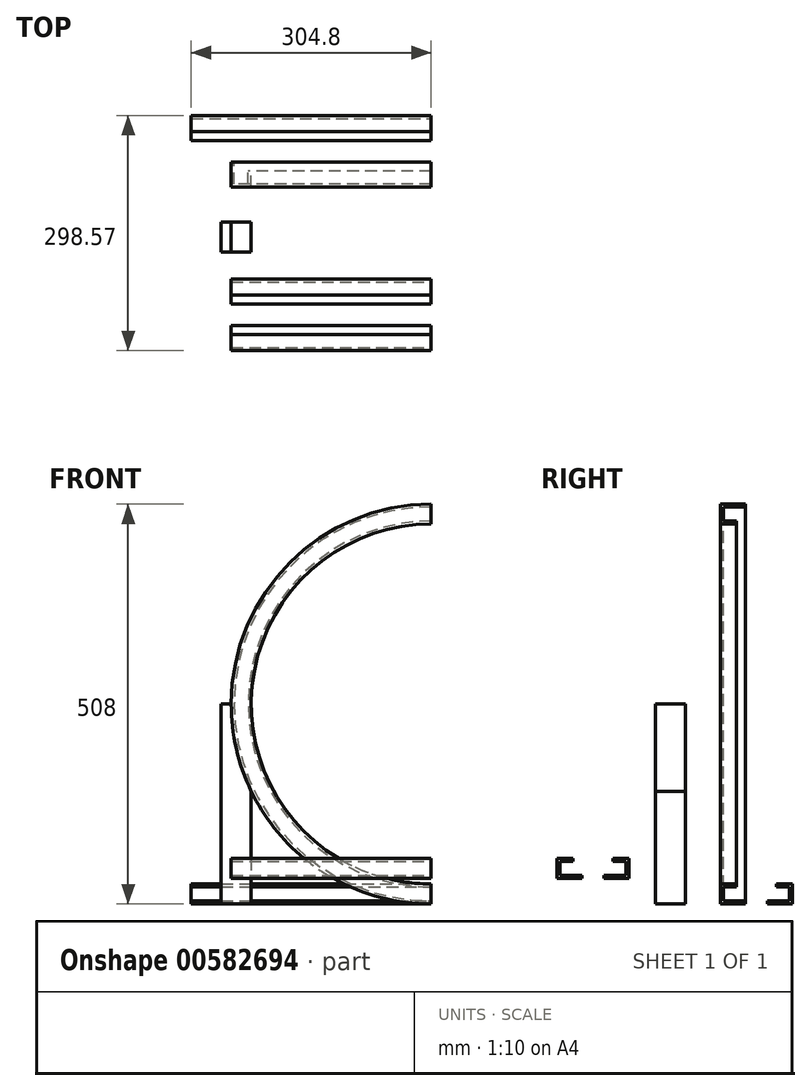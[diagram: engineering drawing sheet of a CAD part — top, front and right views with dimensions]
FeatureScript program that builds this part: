
annotation { "Feature Type Name" : "Feature", "Feature Type Description" : "" }
export const myFeature = defineFeature(function(context is Context, id is Id, definition is map)
    precondition{}
    {
        {
            var Q0;
            Q0=qCreatedBy(makeId("Right.planeOp"),FACE);
            var sketch = newSketch(context, id + "F0", { "sketchPlane" : qUnion([Q0])});
            skLineSegment(sketch, "E0.bottom", {"start": v(-27.94, 21.6) * mm, "end": v(-11.43, 21.6) * mm});
            skLineSegment(sketch, "E0.left", {"start": v(-27.94, 21.6) * mm, "end": v(-27.94, 3.81) * mm});
            skLineSegment(sketch, "E0.right", {"start": v(55.44, 21.6) * mm, "end": v(55.44, 3.81) * mm});
            skLineSegment(sketch, "E1.left", {"start": v(-11.43, 21.6) * mm, "end": v(-11.43, 25.4) * mm});
            skLineSegment(sketch, "E2.bottom", {"start": v(38.93, 25.4) * mm, "end": v(55.44, 25.4) * mm});
            skLineSegment(sketch, "E2.top", {"start": v(38.93, 21.6) * mm, "end": v(55.44, 21.6) * mm});
            skLineSegment(sketch, "E2.left", {"start": v(38.93, 25.4) * mm, "end": v(38.93, 21.6) * mm});
            skLineSegment(sketch, "E3", {"start": v(-11.43, 25.4) * mm, "end": v(-31.75, 25.4) * mm});
            skLineSegment(sketch, "E4", {"start": v(-31.75, 25.4) * mm, "end": v(-31.75, 0) * mm});
            skLineSegment(sketch, "E5", {"start": v(59.25, 0) * mm, "end": v(59.25, 25.4) * mm});
            skLineSegment(sketch, "E6", {"start": v(59.25, 25.4) * mm, "end": v(38.93, 25.4) * mm});
            skLineSegment(sketch, "E7", {"start": v(0, 0) * mm, "end": v(0, 3.81) * mm});
            skLineSegment(sketch, "E8", {"start": v(0, 3.81) * mm, "end": v(-27.94, 3.81) * mm});
            skLineSegment(sketch, "E9", {"start": v(-31.75, 0) * mm, "end": v(0, 0) * mm});
            skLineSegment(sketch, "E10", {"start": v(55.44, 3.81) * mm, "end": v(27.5, 3.81) * mm});
            skLineSegment(sketch, "E11", {"start": v(27.5, 3.81) * mm, "end": v(27.5, 0) * mm});
            skLineSegment(sketch, "E12", {"start": v(27.5, 0) * mm, "end": v(59.25, 0) * mm});
            skSolve(sketch);
        }
        {
            var Q0;
            Q0=qCreatedBy(makeId("Front.planeOp"),FACE);
            var sketch = newSketch(context, id + "F1", { "sketchPlane" : qUnion([Q0])});
            skArc(sketch, "E13", {"start": v(0, 508) * mm, "mid": v(-254, 254) * mm, "end": v(0, 0) * mm});
            skLineSegment(sketch, "E14", {"start": v(0, 254) * mm, "end": v(0, 508) * mm});
            skLineSegment(sketch, "E15", {"start": v(0, 254) * mm, "end": v(-254, 254) * mm});
            skLineSegment(sketch, "E16", {"start": v(0, 254) * mm, "end": v(0, 0) * mm});
            skSolve(sketch);
        }
        {
            var Q0;
            Q0=makeQuery(id+"F0.imprint","IMPRINT",FACE,{"disambiguationData":[TD([[makeQuery(id+"F0.imprint","IMPRINT",EDGE,{"derivedFrom":sQuery(id+"F0.wireOp",EDGE,"E0.bottom")}),1.0]])]});
            var Q1;
            Q1=sQuery(id+"F1.wireOp",EDGE,"E13");
            sweep(context, id + "F2", {"profiles" : qUnion([Q0]), "path" : qUnion([Q1])});
        }
        {
            var Q0;
            Q0=qCreatedBy(makeId("Right.planeOp"),FACE);
            var sketch = newSketch(context, id + "F3", { "sketchPlane" : qUnion([Q0])});
            skLineSegment(sketch, "E17.bottom", {"start": v(-235.5, 53.98) * mm, "end": v(-219, 53.98) * mm});
            skLineSegment(sketch, "E17.left", {"start": v(-235.5, 53.98) * mm, "end": v(-235.5, 36.2) * mm});
            skLineSegment(sketch, "E17.right", {"start": v(-152.13, 53.98) * mm, "end": v(-152.13, 36.2) * mm});
            skLineSegment(sketch, "E18.left", {"start": v(-219, 53.98) * mm, "end": v(-219, 57.8) * mm});
            skLineSegment(sketch, "E19.bottom", {"start": v(-168.64, 57.8) * mm, "end": v(-152.13, 57.8) * mm});
            skLineSegment(sketch, "E19.top", {"start": v(-168.64, 53.98) * mm, "end": v(-152.13, 53.98) * mm});
            skLineSegment(sketch, "E19.left", {"start": v(-168.64, 57.8) * mm, "end": v(-168.64, 53.98) * mm});
            skLineSegment(sketch, "E20", {"start": v(-219, 57.8) * mm, "end": v(-239.32, 57.8) * mm});
            skLineSegment(sketch, "E21", {"start": v(-239.32, 57.8) * mm, "end": v(-239.32, 32.4) * mm});
            skLineSegment(sketch, "E22", {"start": v(-148.32, 32.4) * mm, "end": v(-148.32, 57.8) * mm});
            skLineSegment(sketch, "E23", {"start": v(-148.32, 57.8) * mm, "end": v(-168.64, 57.8) * mm});
            skLineSegment(sketch, "E24", {"start": v(-207.57, 32.4) * mm, "end": v(-207.57, 36.2) * mm});
            skLineSegment(sketch, "E25", {"start": v(-207.57, 36.2) * mm, "end": v(-235.5, 36.2) * mm});
            skLineSegment(sketch, "E26", {"start": v(-239.32, 32.4) * mm, "end": v(-207.57, 32.4) * mm});
            skLineSegment(sketch, "E27", {"start": v(-152.13, 36.2) * mm, "end": v(-180.07, 36.2) * mm});
            skLineSegment(sketch, "E28", {"start": v(-180.07, 36.2) * mm, "end": v(-180.07, 32.4) * mm});
            skLineSegment(sketch, "E29", {"start": v(-180.07, 32.4) * mm, "end": v(-148.32, 32.4) * mm});
            skSolve(sketch);
        }
        {
            var Q0;
            Q0 = qSketchRegion(id + "F3", true);
            extrude(context, id + "F4", {"entities" : qUnion([Q0]), "oppositeDirection" : true, "depth" : 254 * mm, "offsetDistance" : 25.4 * mm});
        }
        {
            var Q0;
            Q0=qCreatedBy(makeId("Front.planeOp"),FACE);
            cPlane(context, id + "F5", {"entities" : qUnion([Q0]), "cplaneType" : CPlaneType.OFFSET, "offset" : 76.2 * mm, "width" : 152.4 * mm, "height" : 152.4 * mm});
        }
        {
            var Q0;
            Q0=qCreatedBy(id+"F5.planeOp",FACE);
            var sketch = newSketch(context, id + "F6", { "sketchPlane" : qUnion([Q0])});
            skLineSegment(sketch, "E30.top", {"start": v(-266.7, 0) * mm, "end": v(-228.6, 0) * mm});
            skLineSegment(sketch, "E30.left", {"start": v(-266.7, 254) * mm, "end": v(-266.7, 0) * mm});
            skLineSegment(sketch, "E30.right", {"start": v(-228.6, 143.28) * mm, "end": v(-228.6, 0) * mm});
            skArc(sketch, "E31", {"start": v(-254, 254) * mm, "mid": v(-247.57, 197.2) * mm, "end": v(-228.6, 143.28) * mm});
            skLineSegment(sketch, "E32", {"start": v(-254, 254) * mm, "end": v(-266.7, 254) * mm});
            skSolve(sketch);
        }
        {
            var Q0;
            Q0=makeQuery(id+"F6.imprint","IMPRINT",FACE,{"disambiguationData":[TD([[makeQuery(id+"F6.imprint","IMPRINT",EDGE,{"derivedFrom":sQuery(id+"F6.wireOp",EDGE,"E30.top")}),1.0]])]});
            extrude(context, id + "F7", {"entities" : qUnion([Q0]), "depth" : 38.1 * mm, "offsetDistance" : 25.4 * mm});
        }
        {
            var Q0;
            Q0=makeQuery(id+"F0.imprint","IMPRINT",FACE,{"disambiguationData":[TD([[makeQuery(id+"F0.imprint","IMPRINT",EDGE,{"derivedFrom":sQuery(id+"F0.wireOp",EDGE,"E0.right")}),1.0]])]});
            extrude(context, id + "F8", {"entities" : qUnion([Q0]), "oppositeDirection" : true, "depth" : 304.8 * mm, "offsetDistance" : 25.4 * mm});
        }
    });
